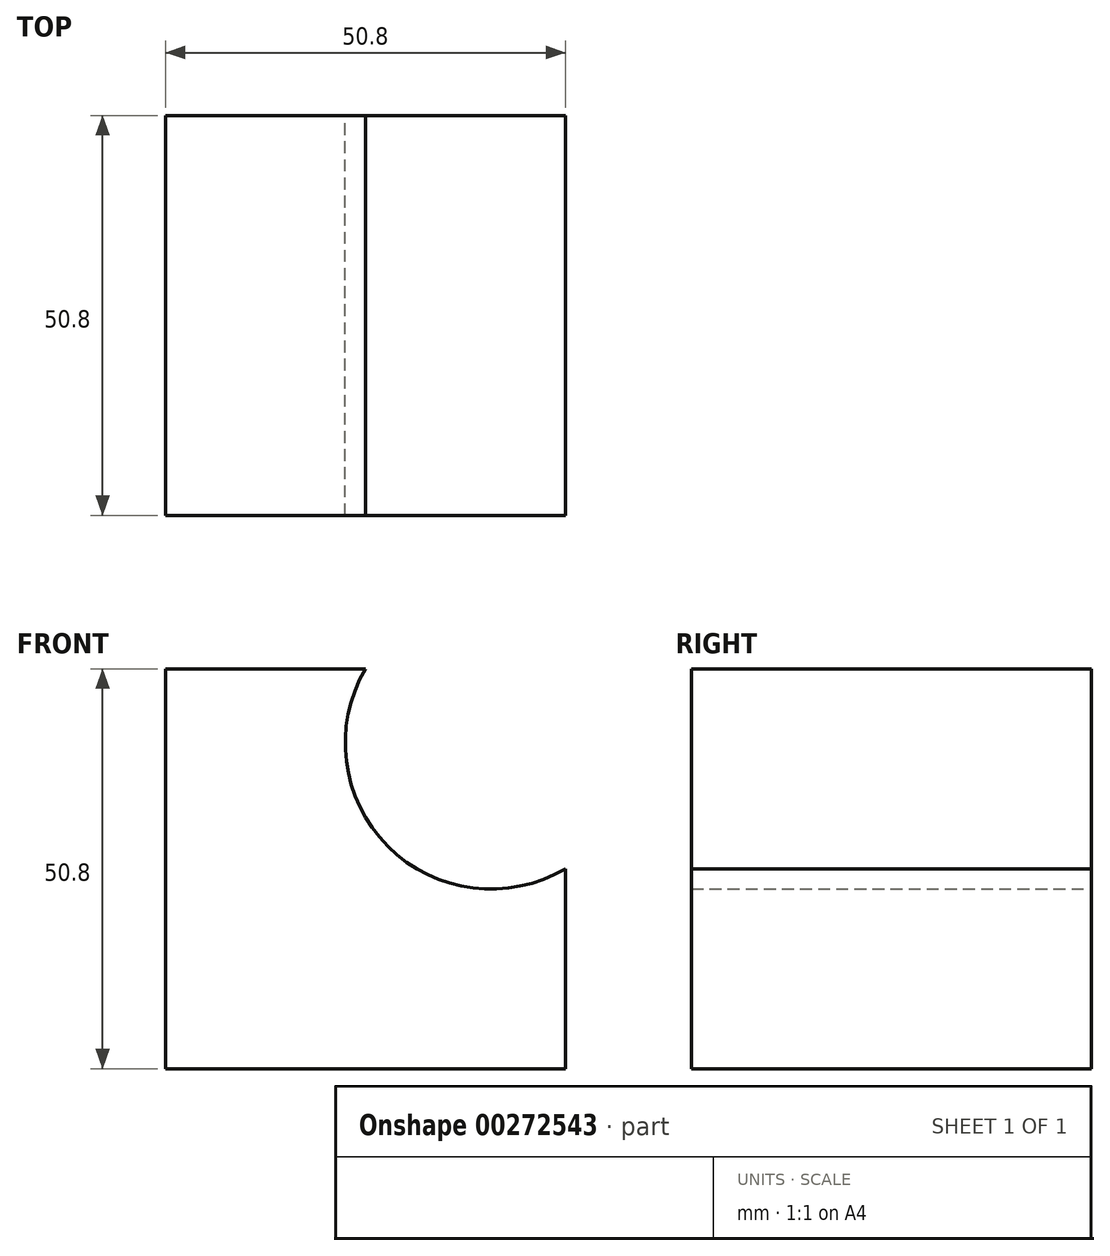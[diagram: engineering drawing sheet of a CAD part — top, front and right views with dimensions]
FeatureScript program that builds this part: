
annotation { "Feature Type Name" : "Feature", "Feature Type Description" : "" }
export const myFeature = defineFeature(function(context is Context, id is Id, definition is map)
    precondition{}
    {
        {
            var Q0;
            Q0=qCreatedBy(makeId("Front.planeOp"),FACE);
            var sketch = newSketch(context, id + "F0", { "sketchPlane" : qUnion([Q0])});
            skLineSegment(sketch, "E0", {"start": v(0, 0) * mm, "end": v(0, 50.8) * mm});
            skLineSegment(sketch, "E1", {"start": v(0, 0) * mm, "end": v(50.8, 0) * mm});
            skLineSegment(sketch, "E2", {"start": v(0, 50.8) * mm, "end": v(25.4, 50.8) * mm});
            skLineSegment(sketch, "E3", {"start": v(50.8, 0) * mm, "end": v(50.8, 25.4) * mm});
            skArc(sketch, "E4", {"start": v(25.4, 50.8) * mm, "mid": v(28.25, 28.25) * mm, "end": v(50.8, 25.4) * mm});
            skSolve(sketch);
        }
        {
            var Q0;
            Q0 = qSketchRegion(id + "F0", true);
            extrude(context, id + "F1", {"entities" : qUnion([Q0]), "depth" : 50.8 * mm});
        }
    });
